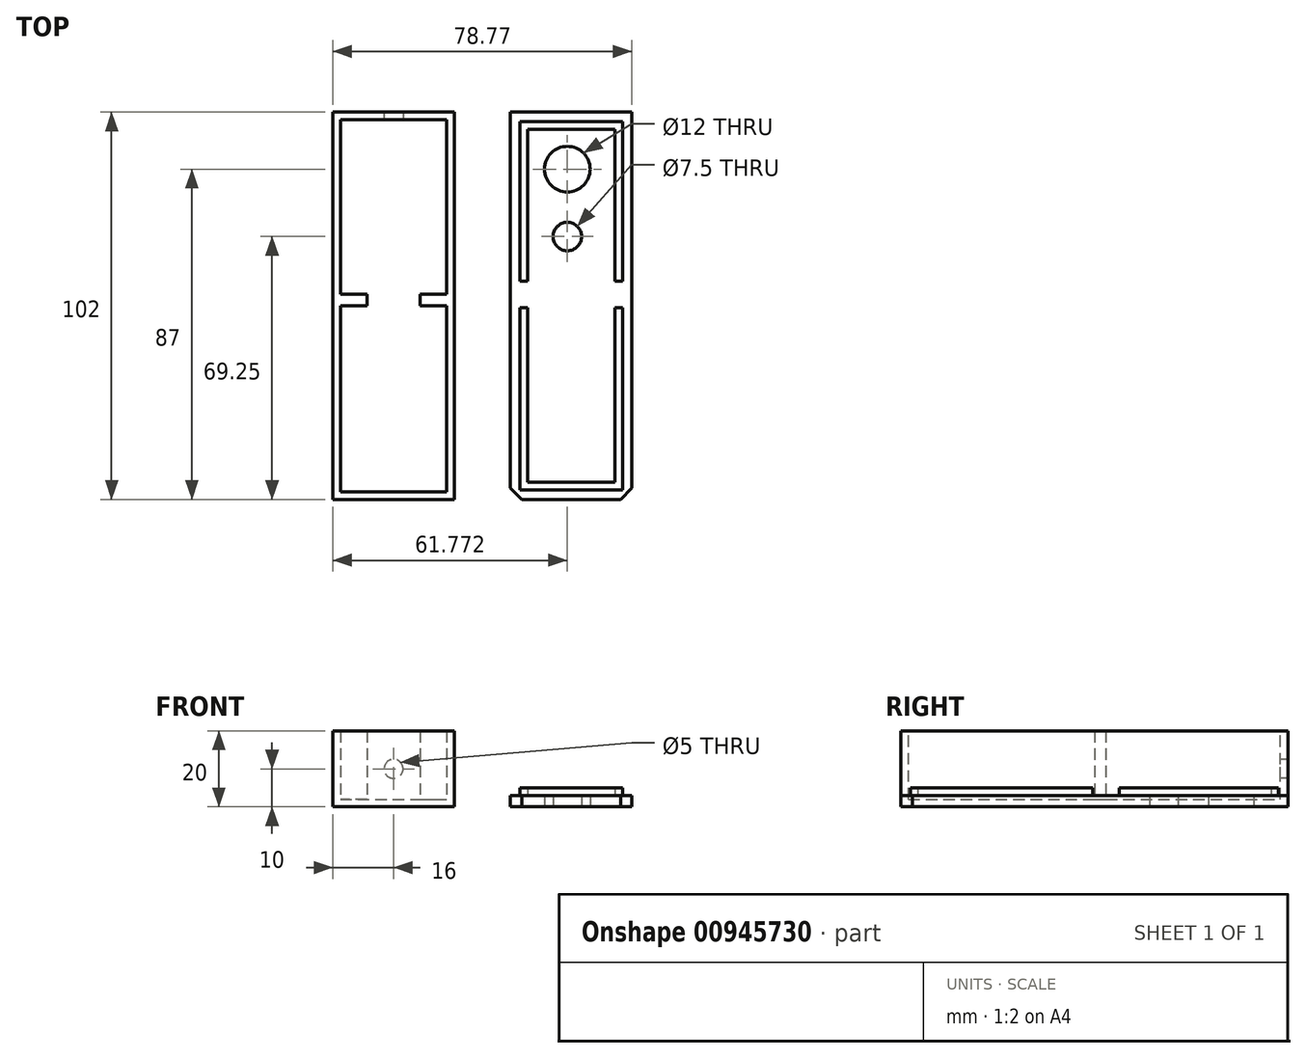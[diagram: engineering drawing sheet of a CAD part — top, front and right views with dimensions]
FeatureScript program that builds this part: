
annotation { "Feature Type Name" : "Feature", "Feature Type Description" : "" }
export const myFeature = defineFeature(function(context is Context, id is Id, definition is map)
    precondition{}
    {
        {
            var Q0;
            Q0=qCreatedBy(makeId("Front.planeOp"),FACE);
            var sketch = newSketch(context, id + "F0", { "sketchPlane" : qUnion([Q0])});
            skLineSegment(sketch, "E0.top", {"start": v(-16, 20) * mm, "end": v(-14, 20) * mm});
            skLineSegment(sketch, "E0.left", {"start": v(-16, 0) * mm, "end": v(-16, 20) * mm});
            skLineSegment(sketch, "E0.right", {"start": v(-14, 2) * mm, "end": v(-14, 20) * mm});
            skLineSegment(sketch, "E1.MirrorCS", {"start": v(14, 2) * mm, "end": v(14, 20) * mm});
            skLineSegment(sketch, "E2.MirrorCS", {"start": v(16, 0) * mm, "end": v(16, 20) * mm});
            skLineSegment(sketch, "E3.MirrorCS", {"start": v(16, 20) * mm, "end": v(14, 20) * mm});
            skLineSegment(sketch, "E4.top", {"start": v(-14, 2) * mm, "end": v(14, 2) * mm});
            skLineSegment(sketch, "E5", {"start": v(-16, 0) * mm, "end": v(16, 0) * mm});
            skSolve(sketch);
        }
        {
            var Q0;
            Q0 = qSketchRegion(id + "F0", true);
            extrude(context, id + "F1", {"entities" : qUnion([Q0]), "depth" : 49 * mm, "offsetDistance" : 25 * mm, "hasSecondDirection" : true, "secondDirectionOppositeDirection" : true, "secondDirectionDepth" : 49 * mm});
        }
        {
            var Q0;
            Q0=qCreatedBy(makeId("Right.planeOp"),FACE);
            var sketch = newSketch(context, id + "F2", { "sketchPlane" : qUnion([Q0])});
            skLineSegment(sketch, "E6.bottom", {"start": v(-49, 0) * mm, "end": v(-51, 0) * mm});
            skLineSegment(sketch, "E6.top", {"start": v(-49, 20) * mm, "end": v(-51, 20) * mm});
            skLineSegment(sketch, "E6.left", {"start": v(-49, 0) * mm, "end": v(-49, 20) * mm});
            skLineSegment(sketch, "E6.right", {"start": v(-51, 0) * mm, "end": v(-51, 20) * mm});
            skLineSegment(sketch, "E7.MirrorCS", {"start": v(51, 0) * mm, "end": v(51, 20) * mm});
            skLineSegment(sketch, "E8.MirrorCS", {"start": v(49, 0) * mm, "end": v(49, 20) * mm});
            skLineSegment(sketch, "E9.MirrorCS", {"start": v(49, 20) * mm, "end": v(51, 20) * mm});
            skLineSegment(sketch, "E10.MirrorCS", {"start": v(49, 0) * mm, "end": v(51, 0) * mm});
            skSolve(sketch);
        }
        {
            var Q0;
            Q0 = qSketchRegion(id + "F2", true);
            extrude(context, id + "F3", {"entities" : qUnion([Q0]), "operationType" : NewBodyOperationType.ADD, "depth" : 16 * mm, "offsetDistance" : 25 * mm, "hasSecondDirection" : true, "secondDirectionOppositeDirection" : true, "secondDirectionDepth" : 16 * mm});
        }
        {
            var Q0;
            Q0=qCreatedBy(makeId("Top.planeOp"),FACE);
            var sketch = newSketch(context, id + "F4", { "sketchPlane" : qUnion([Q0])});
            skLineSegment(sketch, "E11.bottom", {"start": v(-14, 3) * mm, "end": v(-7, 3) * mm});
            skLineSegment(sketch, "E11.top", {"start": v(-14, 0) * mm, "end": v(-7, 0) * mm});
            skLineSegment(sketch, "E11.left", {"start": v(-14, 3) * mm, "end": v(-14, 0) * mm});
            skLineSegment(sketch, "E11.right", {"start": v(-7, 3) * mm, "end": v(-7, 0) * mm});
            skLineSegment(sketch, "E12.MirrorCS", {"start": v(14, 3) * mm, "end": v(14, 0) * mm});
            skLineSegment(sketch, "E13.MirrorCS", {"start": v(14, 0) * mm, "end": v(7, 0) * mm});
            skLineSegment(sketch, "E14.MirrorCS", {"start": v(7, 3) * mm, "end": v(7, 0) * mm});
            skLineSegment(sketch, "E15.MirrorCS", {"start": v(14, 3) * mm, "end": v(7, 3) * mm});
            skSolve(sketch);
        }
        {
            var Q0;
            Q0 = qSketchRegion(id + "F4", true);
            extrude(context, id + "F5", {"entities" : qUnion([Q0]), "operationType" : NewBodyOperationType.ADD, "depth" : 20 * mm, "offsetDistance" : 25 * mm});
        }
        {
            var Q0;
            Q0=qCreatedBy(makeId("Front.planeOp"),FACE);
            var sketch = newSketch(context, id + "F6", { "sketchPlane" : qUnion([Q0])});
            skCircle(sketch, "E16", {"center": v(0, 10) * mm, "radius": 2.5 * mm});
            skSolve(sketch);
        }
        {
            var Q0;
            Q0=makeQuery(id+"F6.imprint","IMPRINT",FACE,{"disambiguationData":[TD([[makeQuery(id+"F6.imprint","IMPRINT",EDGE,{"derivedFrom":sQuery(id+"F6.wireOp",EDGE,"E16")}),1.0]])]});
            extrude(context, id + "F7", {"entities" : qUnion([Q0]), "operationType" : NewBodyOperationType.REMOVE, "endBound" : BoundingType.THROUGH_ALL, "oppositeDirection" : true, "depth" : 25 * mm, "offsetDistance" : 25 * mm});
        }
        {
            var Q0;
            Q0=qCreatedBy(makeId("Top.planeOp"),FACE);
            var sketch = newSketch(context, id + "F8", { "sketchPlane" : qUnion([Q0])});
            skLineSegment(sketch, "E17.bottom", {"start": v(30.77, 51) * mm, "end": v(62.77, 51) * mm});
            skLineSegment(sketch, "E17.top", {"start": v(30.77, -51) * mm, "end": v(62.77, -51) * mm});
            skLineSegment(sketch, "E17.left", {"start": v(30.77, 51) * mm, "end": v(30.77, -51) * mm});
            skLineSegment(sketch, "E17.right", {"start": v(62.77, 51) * mm, "end": v(62.77, -51) * mm});
            skLineSegment(sketch, "E18.bottom", {"start": v(33.27, 48.5) * mm, "end": v(60.27, 48.5) * mm});
            skLineSegment(sketch, "E18.top", {"start": v(33.27, -48.5) * mm, "end": v(60.27, -48.5) * mm});
            skLineSegment(sketch, "E18.left", {"start": v(33.27, 48.5) * mm, "end": v(33.27, 6.5) * mm});
            skLineSegment(sketch, "E18.right", {"start": v(60.27, 48.5) * mm, "end": v(60.27, 6.5) * mm});
            skLineSegment(sketch, "E19.bottom", {"start": v(35.27, 46.5) * mm, "end": v(58.27, 46.5) * mm});
            skLineSegment(sketch, "E19.top", {"start": v(35.27, -46.5) * mm, "end": v(58.27, -46.5) * mm});
            skLineSegment(sketch, "E19.left", {"start": v(35.27, 46.5) * mm, "end": v(35.27, 6.5) * mm});
            skLineSegment(sketch, "E19.right", {"start": v(58.27, 46.5) * mm, "end": v(58.27, 6.5) * mm});
            skLineSegment(sketch, "E20", {"start": v(33.27, -0.5) * mm, "end": v(35.27, -0.5) * mm});
            skLineSegment(sketch, "E21", {"start": v(33.27, 6.5) * mm, "end": v(35.27, 6.5) * mm});
            skLineSegment(sketch, "E22", {"start": v(58.27, 6.5) * mm, "end": v(60.27, 6.5) * mm});
            skLineSegment(sketch, "E23", {"start": v(58.27, -0.5) * mm, "end": v(60.27, -0.5) * mm});
            skLineSegment(sketch, "E24.trimOffspring", {"start": v(33.27, -0.5) * mm, "end": v(33.27, -48.5) * mm});
            skLineSegment(sketch, "E25.trimOffspring", {"start": v(35.27, -0.5) * mm, "end": v(35.27, -46.5) * mm});
            skLineSegment(sketch, "E26.trimOffspring", {"start": v(58.27, -0.5) * mm, "end": v(58.27, -46.5) * mm});
            skLineSegment(sketch, "E27.trimOffspring", {"start": v(60.27, -0.5) * mm, "end": v(60.27, -48.5) * mm});
            skLineSegment(sketch, "E28.bottom", {"start": v(42.77, -51) * mm, "end": v(50.77, -51) * mm});
            skLineSegment(sketch, "E28.top", {"start": v(42.77, -56) * mm, "end": v(50.77, -56) * mm});
            skLineSegment(sketch, "E28.left", {"start": v(42.77, -51) * mm, "end": v(42.77, -56) * mm});
            skLineSegment(sketch, "E28.right", {"start": v(50.77, -51) * mm, "end": v(50.77, -56) * mm});
            skCircle(sketch, "E29", {"center": v(45.77, 36) * mm, "radius": 6 * mm});
            skCircle(sketch, "E30", {"center": v(45.77, 18.25) * mm, "radius": 3.75 * mm});
            skSolve(sketch);
        }
        {
            var Q0;
            Q0=makeQuery(id+"F8.imprint","IMPRINT",FACE,{"disambiguationData":[TD([[makeQuery(id+"F8.imprint","IMPRINT",EDGE,{"derivedFrom":sQuery(id+"F8.wireOp",EDGE,"E17.bottom")}),-1.0]])]});
            var Q1;
            Q1=makeQuery(id+"F8.imprint","IMPRINT",FACE,{"disambiguationData":[TD([[makeQuery(id+"F8.imprint","IMPRINT",EDGE,{"derivedFrom":sQuery(id+"F8.wireOp",EDGE,"E28.bottom")}),-1.0]])]});
            extrude(context, id + "F9", {"entities" : qUnion([Q0, Q1]), "depth" : 3 * mm, "offsetDistance" : 25 * mm});
        }
        {
            var Q0;
            Q0=makeQuery(id+"F8.imprint","IMPRINT",FACE,{"disambiguationData":[TD([[makeQuery(id+"F8.imprint","IMPRINT",EDGE,{"derivedFrom":sQuery(id+"F8.wireOp",EDGE,"E18.bottom")}),-1.0]])]});
            var Q1;
            Q1=makeQuery(id+"F8.imprint","IMPRINT",FACE,{"disambiguationData":[TD([[makeQuery(id+"F8.imprint","IMPRINT",EDGE,{"derivedFrom":sQuery(id+"F8.wireOp",EDGE,"E18.top")}),1.0]])]});
            extrude(context, id + "F10", {"entities" : qUnion([Q0, Q1]), "operationType" : NewBodyOperationType.ADD, "depth" : 5 * mm, "offsetDistance" : 25 * mm});
        }
        {
            var Q0;
            Q0=makeQuery(id+"F5.opExtrude","SWEPT_EDGE",EDGE,{"disambiguationData":[OSD([sQuery(id+"F4.wireOp",EDGE,"E11.bottom"),sQuery(id+"F4.wireOp",EDGE,"E11.left")])]});
            var Q1;
            Q1=makeQuery(id+"F5.opExtrude","SWEPT_EDGE",EDGE,{"disambiguationData":[OSD([sQuery(id+"F4.wireOp",EDGE,"E12.MirrorCS"),sQuery(id+"F4.wireOp",EDGE,"E15.MirrorCS")])]});
            var Q2;
            Q2=makeQuery(id+"F9.opExtrude","SWEPT_EDGE",EDGE,{"disambiguationData":[OSD([sQuery(id+"F8.wireOp",EDGE,"E17.top"),sQuery(id+"F8.wireOp",EDGE,"E28.bottom"),sQuery(id+"F8.wireOp",EDGE,"E28.right")])]});
            var Q3;
            Q3=makeQuery(id+"F9.opExtrude","SWEPT_EDGE",EDGE,{"disambiguationData":[OSD([sQuery(id+"F8.wireOp",EDGE,"E17.top"),sQuery(id+"F8.wireOp",EDGE,"E28.bottom"),sQuery(id+"F8.wireOp",EDGE,"E28.left")])]});
            chamfer(context, id + "F11", {"entities" : qUnion([Q0, Q1, Q2, Q3]), "width" : 3 * mm, "tangentPropagation" : true});
        }
    });
